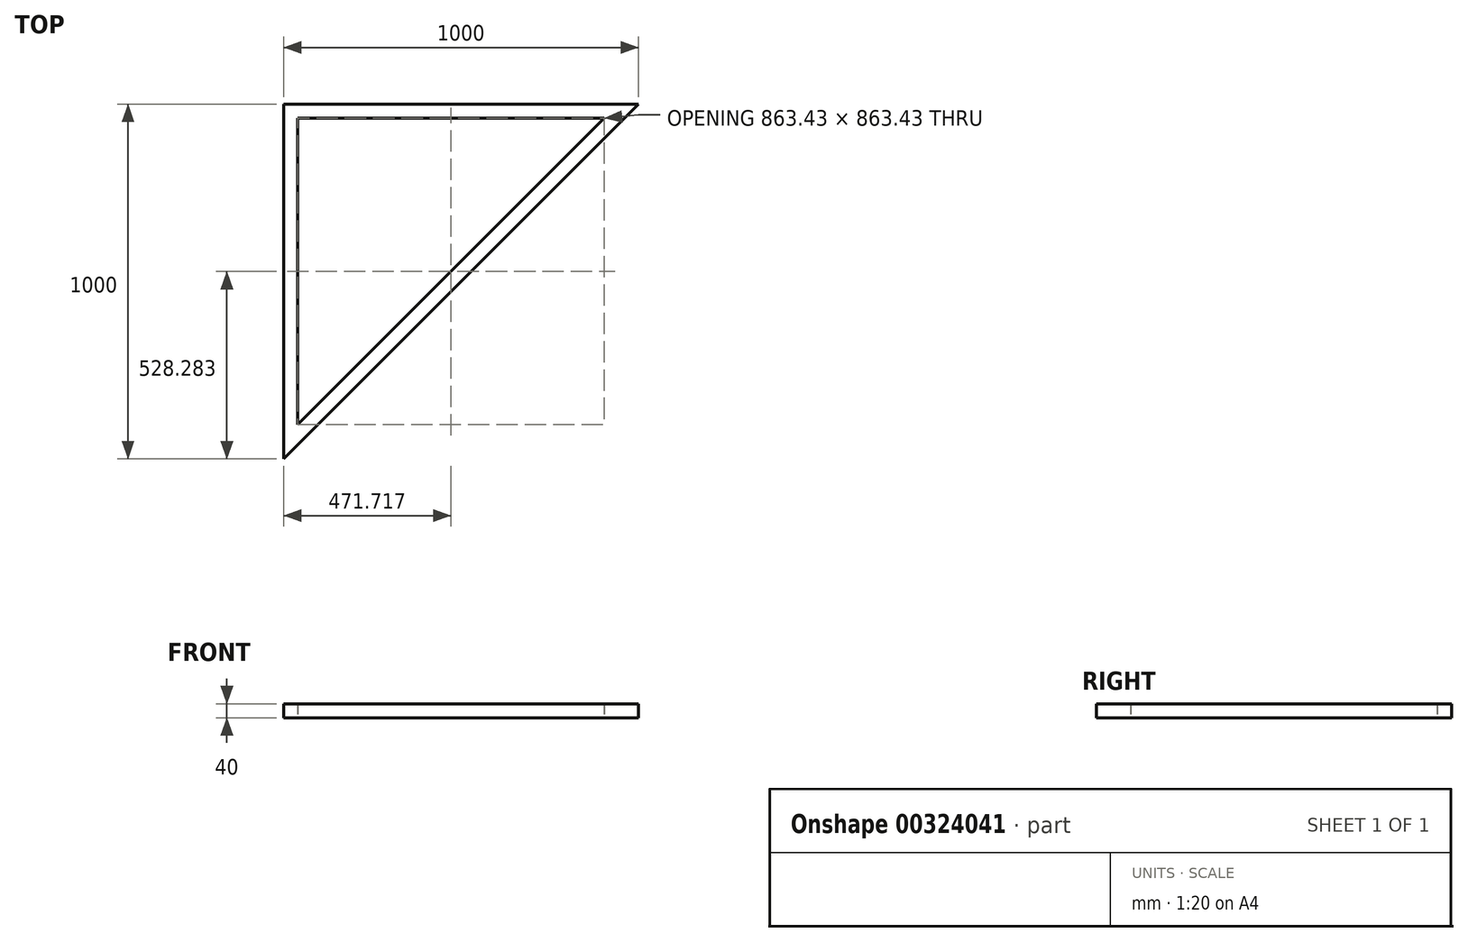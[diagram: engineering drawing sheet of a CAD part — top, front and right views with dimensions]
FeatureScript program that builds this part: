
annotation { "Feature Type Name" : "Feature", "Feature Type Description" : "" }
export const myFeature = defineFeature(function(context is Context, id is Id, definition is map)
    precondition{}
    {
        {
            var Q0;
            Q0=qCreatedBy(makeId("Top.planeOp"),FACE);
            var sketch = newSketch(context, id + "F0", { "sketchPlane" : qUnion([Q0])});
            skLineSegment(sketch, "E0.top", {"start": v(-733.27, 501.6) * mm, "end": v(266.73, 501.6) * mm});
            skLineSegment(sketch, "E0.left", {"start": v(-733.27, -498.4) * mm, "end": v(-733.27, 501.6) * mm});
            skLineSegment(sketch, "E1", {"start": v(-733.27, -498.4) * mm, "end": v(266.73, 501.6) * mm});
            skLineSegment(sketch, "E2.0", {"start": v(-693.27, -401.83) * mm, "end": v(170.16, 461.6) * mm});
            skLineSegment(sketch, "E2.1", {"start": v(-693.27, -401.83) * mm, "end": v(-693.27, 461.6) * mm});
            skLineSegment(sketch, "E2.2", {"start": v(-693.27, 461.6) * mm, "end": v(170.16, 461.6) * mm});
            skSolve(sketch);
        }
        {
            var Q0;
            Q0 = qSketchRegion(id + "F0", true);
            extrude(context, id + "F1", {"entities" : qUnion([Q0]), "depth" : 40 * mm});
        }
    });
